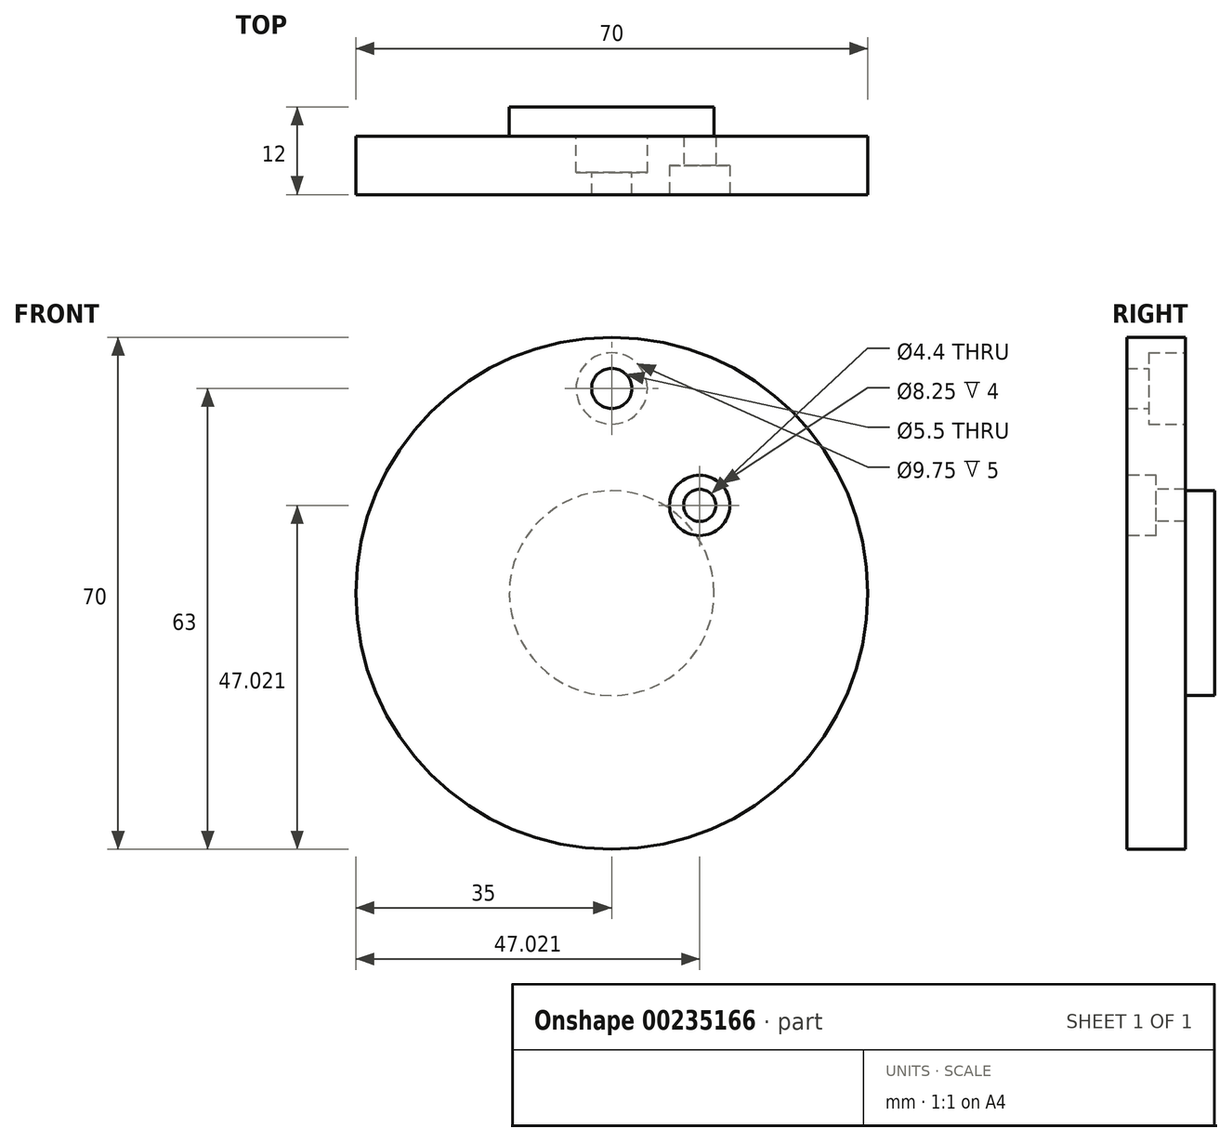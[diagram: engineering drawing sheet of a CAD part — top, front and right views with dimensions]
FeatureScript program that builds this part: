
annotation { "Feature Type Name" : "Feature", "Feature Type Description" : "" }
export const myFeature = defineFeature(function(context is Context, id is Id, definition is map)
    precondition{}
    {
        {
            var Q0;
            Q0=qCreatedBy(makeId("Front.planeOp"),FACE);
            var sketch = newSketch(context, id + "F0", { "sketchPlane" : qUnion([Q0])});
            skCircle(sketch, "E0", {"center": v(0, 0) * mm, "radius": 17 * mm, "construction": true});
            skCircle(sketch, "E1", {"center": v(0, 0) * mm, "radius": 28 * mm, "construction": true});
            skCircle(sketch, "E2", {"center": v(0, 0) * mm, "radius": 14 * mm});
            skCircle(sketch, "E3", {"center": v(0, 0) * mm, "radius": 35 * mm});
            skLineSegment(sketch, "E4", {"start": v(0, 0) * mm, "end": v(12.02, 12.02) * mm, "construction": true});
            skPoint(sketch, "E5", {"position": v(0, 28) * mm});
            skCircle(sketch, "E6", {"center": v(12.02, 12.02) * mm, "radius": 4.12 * mm, "construction": true});
            skCircle(sketch, "E7", {"center": v(0, 28) * mm, "radius": 4.88 * mm, "construction": true});
            skSolve(sketch);
        }
        {
            var Q0;
            Q0=makeQuery(id+"F0.imprint","IMPRINT",FACE,{"disambiguationData":[TD([[makeQuery(id+"F0.imprint","IMPRINT",EDGE,{"derivedFrom":sQuery(id+"F0.wireOp",EDGE,"E2")}),-1.0]])]});
            var Q1;
            Q1=makeQuery(id+"F0.imprint","IMPRINT",FACE,{"disambiguationData":[TD([[makeQuery(id+"F0.imprint","IMPRINT",EDGE,{"derivedFrom":sQuery(id+"F0.wireOp",EDGE,"E2")}),1.0]])]});
            extrude(context, id + "F1", {"entities" : qUnion([Q0, Q1]), "depth" : 8 * mm});
        }
        {
            var Q0;
            Q0=makeQuery(id+"F0.imprint","IMPRINT",FACE,{"disambiguationData":[TD([[makeQuery(id+"F0.imprint","IMPRINT",EDGE,{"derivedFrom":sQuery(id+"F0.wireOp",EDGE,"E2")}),1.0]])]});
            extrude(context, id + "F2", {"entities" : qUnion([Q0]), "operationType" : NewBodyOperationType.ADD, "oppositeDirection" : true, "depth" : 4 * mm});
        }
        {
            var Q0;
            Q0=makeQuery(id+"F1.opExtrude","CAP_FACE",FACE,{"disambiguationData":[OSD([sQuery(id+"F0.wireOp",EDGE,"E3")])],"isStart":false});
            var sketch = newSketch(context, id + "F3", { "sketchPlane" : qUnion([Q0])});
            skPoint(sketch, "E8.0", {"position": v(12.02, 12.02) * mm});
            skSolve(sketch);
        }
        {
            var Q0;
            Q0=sQuery(id+"F3.wireOp",VERTEX,"E8.0");
            var Q1;
            Q1=makeQuery(id+"F1.opExtrude","SWEPT_BODY",BODY,{"disambiguationData":[OSD([sQuery(id+"F0.wireOp",EDGE,"E3")])]});
            hole(context, id + "F4", {"style" : HoleStyle.C_BORE, "endStyle" : HoleEndStyle.THROUGH, "standardTappedOrClearance" : lookupTablePath({ "standard" : "ISO", "fit" : "Normal", "size" : "M4", "type" : "Clearance" }), "standardBlindInLast" : lookupTablePath({ "fit" : "Standard", "standard" : "ISO", "size" : "M4", "type" : "Clearance" }), "holeDiameter" : 4.4 * mm, "cBoreDiameter" : 8.25 * mm, "cBoreDepth" : 4 * mm, "locations" : qUnion([Q0]), "scope" : qUnion([Q1]), "isTappedThrough" : true});
        }
        {
            var Q0;
            Q0=sQuery(id+"F0.wireOp",VERTEX,"E5");
            var Q1;
            Q1=makeQuery(id+"F1.opExtrude","SWEPT_BODY",BODY,{"disambiguationData":[OSD([sQuery(id+"F0.wireOp",EDGE,"E3")])]});
            hole(context, id + "F5", {"style" : HoleStyle.C_BORE, "endStyle" : HoleEndStyle.THROUGH, "oppositeDirection" : true, "standardTappedOrClearance" : lookupTablePath({ "standard" : "ISO", "fit" : "Normal", "size" : "M5", "type" : "Clearance" }), "standardBlindInLast" : lookupTablePath({ "fit" : "Standard", "standard" : "ISO", "size" : "M5", "type" : "Clearance" }), "holeDiameter" : 5.5 * mm, "cBoreDiameter" : 9.75 * mm, "cBoreDepth" : 5 * mm, "locations" : qUnion([Q0]), "scope" : qUnion([Q1]), "isTappedThrough" : true});
        }
    });
